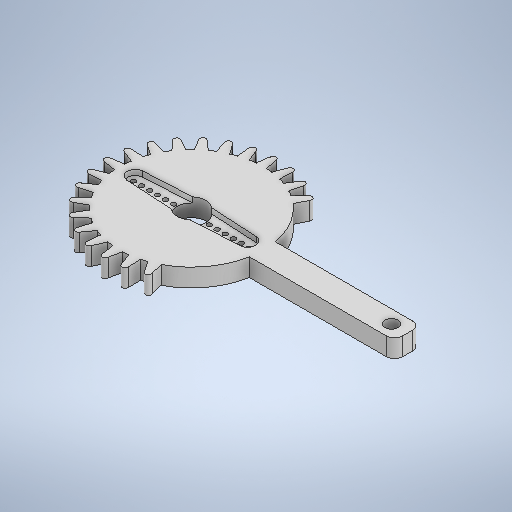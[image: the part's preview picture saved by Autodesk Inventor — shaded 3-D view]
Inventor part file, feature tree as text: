
AUTODESK INVENTOR PART (.ipt)
format: ipt  version: 2025.1 (Build 291241020, 241B)  size: 726,528 bytes
history: native  units: in
note: dims shown in document units (in); Inventor stores cm internally (conversion verified against a paired STEP export)
features: extrude x12, sketch x12, other x3, fillet x2, pattern_circular x1
ambient origin geometry x8: Origin, YZ Plane, XZ Plane, XY Plane, X Axis, Y Axis, Z Axis, Center Point
bodies: Solid1 (feature_tree)
feature tree (30):
  other  "servoMoldAssembly.iam"
  other  "block.ipt:1"
  other  "sg90horn.ipt:1"
  extrude  "Extrusion1"  Depth=0.3937in TaperAngle=0.0deg
  extrude  "Extrusion2"  Depth=0.3937in TaperAngle=0.0deg
  extrude  "Extrusion3"  Depth=0.0591in TaperAngle=0.0deg
  extrude  "Extrusion4"  Depth=0.0591in TaperAngle=0.0deg
  extrude  "Extrusion5"  Depth=1.9685in
  extrude  "Extrusion6"  Depth=0.3937in TaperAngle=0.0deg
  extrude  "Extrusion7"  Depth=0.3937in
  extrude  "Extrusion8"  Depth=0.0591in
  extrude  "Extrusion9"  Depth=0.3937in TaperAngle=240.0deg
  pattern_circular  "Circular Pattern1"  [2 undecoded]
  extrude  "Extrusion10"  Depth=0.0787in TaperAngle=0.0deg
  extrude  "Extrusion11"  Depth=0.0787in
  fillet  "Fillet1"  Radius=0.2362in
  extrude  "Extrusion12"  Depth=0.0787in
  fillet  "Fillet2"  [1 undecoded]
  sketch  "Sketch3"  dims[d0=0.3937in d1=0.3937in d2=0.0in]
  sketch  "Sketch4"  dims[d3=0.2795in d4=0.3937in d5=0.0in]
  sketch  "Sketch5"  dims[d6=0.0591in d7=0.0in d8=0.0591in d9=0.0in]
  sketch  "Sketch6"  dims[d10=0.0591in d11=0.0in d12=0.0591in d13=0.0in]
  sketch  "Sketch7"  dims[d14=1.4173in d15=1.9685in]
  sketch  "Sketch8"  dims[d16=0.0in d17=0.3937in d18=0.0in]
  sketch  "Sketch9"  dims[d19=0.3937in d20=0.0in d21=0.0984in]
  sketch  "Sketch10"  dims[d22=0.1181in d23=0.0591in]
  sketch  "Sketch11"  dims[d24=0.3937in d25=0.0in d26=7.874in d27=240.0deg]
  sketch  "Sketch12"  dims[d29=0.2362in d30=0.0in]
  sketch  "Sketch13"  dims[d31=0.2362in]
  sketch  "Sketch14"  dims[d32=0.1299in d33=0.0787in d34=0.2362in d35=0.0in d36=0.0787in d37=0.2362in d38=0.0in d39=0.0787in]
note: 3 required parameter values undecoded (feature->parameter linkage not recoverable at this tier; creation-order binding heuristic only, values carry confidence <= 0.55)
